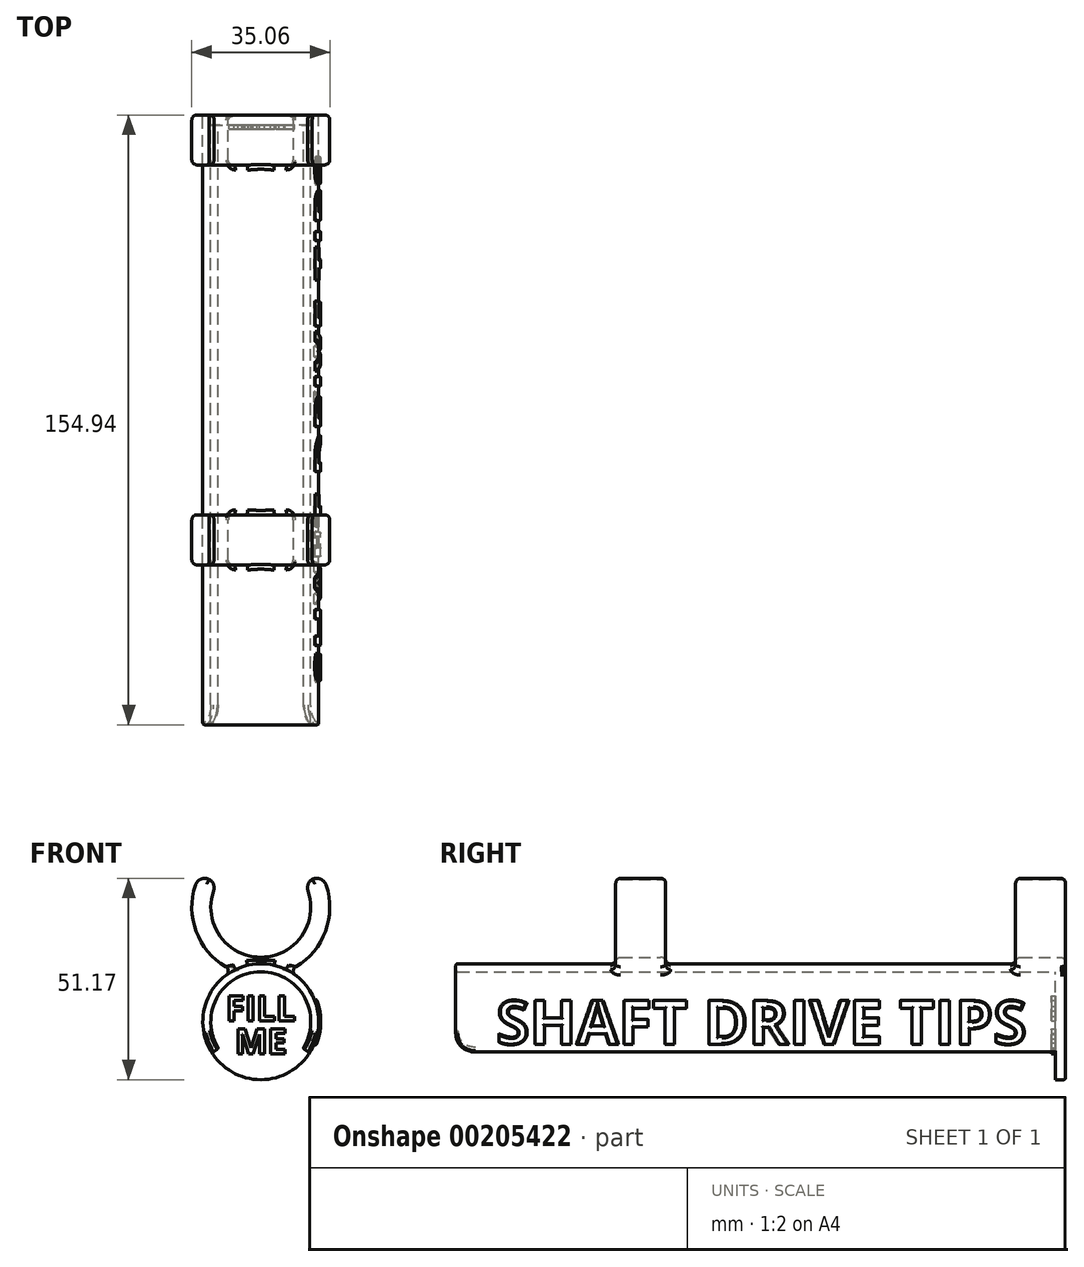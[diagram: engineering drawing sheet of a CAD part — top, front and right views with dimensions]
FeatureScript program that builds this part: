
annotation { "Feature Type Name" : "Feature", "Feature Type Description" : "" }
export const myFeature = defineFeature(function(context is Context, id is Id, definition is map)
    precondition{}
    {
        {
            var Q0;
            Q0=qCreatedBy(makeId("Front.planeOp"),FACE);
            var sketch = newSketch(context, id + "F0", { "sketchPlane" : qUnion([Q0])});
            skCircle(sketch, "E0", {"center": v(0, 0) * mm, "radius": 14.73 * mm});
            skSolve(sketch);
        }
        {
            var Q0;
            Q0 = qSketchRegion(id + "F0", true);
            extrude(context, id + "F1", {"entities" : qUnion([Q0]), "depth" : 2.54 * mm});
        }
        {
            var Q0;
            Q0=makeQuery(id+"F1.opExtrude","CAP_FACE",FACE,{"disambiguationData":[OSD([sQuery(id+"F0.wireOp",EDGE,"E0")])],"isStart":false});
            var sketch = newSketch(context, id + "F2", { "sketchPlane" : qUnion([Q0])});
            skArc(sketch, "E1", {"start": v(12.43, -7.91) * mm, "mid": v(0, 14.73) * mm, "end": v(-12.43, -7.91) * mm});
            skArc(sketch, "E2", {"start": v(10.71, -6.82) * mm, "mid": v(0, 12.7) * mm, "end": v(-10.71, -6.82) * mm});
            skLineSegment(sketch, "E3", {"start": v(-10.71, -6.82) * mm, "end": v(-12.43, -7.91) * mm});
            skLineSegment(sketch, "E4", {"start": v(12.43, -7.91) * mm, "end": v(10.71, -6.82) * mm});
            skSolve(sketch);
        }
        {
            var Q0;
            Q0 = qSketchRegion(id + "F2", true);
            extrude(context, id + "F3", {"entities" : qUnion([Q0]), "operationType" : NewBodyOperationType.ADD, "depth" : 152.4 * mm});
        }
        {
            var Q0;
            Q0=makeQuery(id+"F3.opExtrude","CAP_EDGE",EDGE,{"disambiguationData":[OSD([sQuery(id+"F2.wireOp",EDGE,"E3")])],"isStart":false});
            var Q1;
            Q1=makeQuery(id+"F3.opExtrude","CAP_EDGE",EDGE,{"disambiguationData":[OSD([sQuery(id+"F2.wireOp",EDGE,"E4")])],"isStart":false});
            fillet(context, id + "F4", {"entities" : qUnion([Q0, Q1]), "radius" : 5.08 * mm, "tangentPropagation" : true, "allowEdgeOverflow" : false});
        }
        {
            var Q0;
            Q0=qCreatedBy(makeId("Right.planeOp"),FACE);
            var sketch = newSketch(context, id + "F5", { "sketchPlane" : qUnion([Q0])});
            skText(sketch, "E5", { "text": "SHAFT DRIVE TIPS", "fontName": "OpenSans-Bold.ttf"});
            const initialGuessF5  = {"E5": [-0.14472, -0.00573, 1, 0, 0.01118]};
            skSetInitialGuess(sketch, initialGuessF5);
            skSolve(sketch);
        }
        {
            var Q0;
            Q0 = qSketchRegion(id + "F5", true);
            extrude(context, id + "F6", {"entities" : qUnion([Q0]), "operationType" : NewBodyOperationType.ADD, "depth" : 25.4 * mm});
        }
        {
            var Q0;
            Q0=makeQuery(id+"F1.opExtrude","CAP_FACE",FACE,{"disambiguationData":[OSD([sQuery(id+"F0.wireOp",EDGE,"E0")])],"isStart":false});
            var sketch = newSketch(context, id + "F7", { "sketchPlane" : qUnion([Q0])});
            skCircle(sketch, "E6", {"center": v(0, 0) * mm, "radius": 12.7 * mm});
            skSolve(sketch);
        }
        {
            var Q0;
            Q0 = qSketchRegion(id + "F7", true);
            extrude(context, id + "F8", {"entities" : qUnion([Q0]), "operationType" : NewBodyOperationType.REMOVE, "depth" : 177.8 * mm});
        }
        {
            var Q0;
            Q0=makeQuery(id+"F1.opExtrude","CAP_FACE",FACE,{"disambiguationData":[OSD([sQuery(id+"F0.wireOp",EDGE,"E0")])],"isStart":false});
            var sketch = newSketch(context, id + "F9", { "sketchPlane" : qUnion([Q0])});
            skCircle(sketch, "E7", {"center": v(0, 0) * mm, "radius": 15.24 * mm});
            skCircle(sketch, "E8", {"center": v(0, 0) * mm, "radius": 65.87 * mm});
            skSolve(sketch);
        }
        {
            var Q0;
            Q0 = qSketchRegion(id + "F9", true);
            extrude(context, id + "F10", {"entities" : qUnion([Q0]), "operationType" : NewBodyOperationType.REMOVE, "depth" : 152.4 * mm});
        }
        {
            var Q0;
            Q0=makeQuery(id+"F3.opExtrude","SWEPT_EDGE",EDGE,{"disambiguationData":[OSD([sQuery(id+"F2.wireOp",EDGE,"E2"),sQuery(id+"F2.wireOp",EDGE,"E3")])]});
            var Q1;
            Q1=makeQuery(id+"F4.opFillet","BLEND_EDGE",EDGE,{"blendedFrom":[makeQuery(id+"F3.opExtrude","CAP_EDGE",EDGE,{"disambiguationData":[OSD([sQuery(id+"F2.wireOp",EDGE,"E4")])],"isStart":false}),makeQuery(id+"F3.boolean.opBoolean","MERGE",FACE,{"derivedFrom":[makeQuery(id+"F1.opExtrude","SWEPT_FACE",FACE,{"disambiguationData":[OSD([sQuery(id+"F0.wireOp",EDGE,"E0")])]}),makeQuery(id+"F3.opExtrude","SWEPT_FACE",FACE,{"disambiguationData":[OSD([sQuery(id+"F2.wireOp",EDGE,"E1")])]})]})],"blendedInto":[makeQuery(id+"F3.boolean.opBoolean","MERGE",FACE,{"derivedFrom":[makeQuery(id+"F1.opExtrude","SWEPT_FACE",FACE,{"disambiguationData":[OSD([sQuery(id+"F0.wireOp",EDGE,"E0")])]}),makeQuery(id+"F3.opExtrude","SWEPT_FACE",FACE,{"disambiguationData":[OSD([sQuery(id+"F2.wireOp",EDGE,"E1")])]})]})]});
            var Q2;
            Q2=makeQuery(id+"F3.opExtrude","CAP_EDGE",EDGE,{"disambiguationData":[OSD([sQuery(id+"F2.wireOp",EDGE,"E2")])],"isStart":true});
            var Q3;
            Q3=makeQuery(id+"F1.opExtrude","CAP_EDGE",EDGE,{"disambiguationData":[OSD([sQuery(id+"F0.wireOp",EDGE,"E0")])],"isStart":true});
            fillet(context, id + "F11", {"entities" : qUnion([Q0, Q1, Q2, Q3]), "radius" : 0.5 * mm, "tangentPropagation" : true, "allowEdgeOverflow" : false});
        }
        {
            var Q0;
            Q0=qCreatedBy(makeId("Front.planeOp"),FACE);
            cPlane(context, id + "F12", {"entities" : qUnion([Q0]), "cplaneType" : CPlaneType.OFFSET, "offset" : 101.6 * mm, "width" : 152.4 * mm, "height" : 152.4 * mm});
        }
        {
            var Q0;
            Q0=qCreatedBy(makeId("Front.planeOp"),FACE);
            var sketch = newSketch(context, id + "F13", { "sketchPlane" : qUnion([Q0])});
            skArc(sketch, "E9", {"start": v(-11.15, 35.14) * mm, "mid": v(0, 16.37) * mm, "end": v(11.15, 35.14) * mm});
            skArc(sketch, "E10", {"start": v(5.72, 12.5) * mm, "mid": v(16.34, 22.73) * mm, "end": v(15.4, 37.45) * mm});
            skArc(sketch, "E11", {"start": v(5.72, 12.5) * mm, "mid": v(0, 13.74) * mm, "end": v(-5.72, 12.5) * mm});
            skLineSegment(sketch, "E12", {"start": v(-11.15, 35.14) * mm, "end": v(-15.4, 37.45) * mm});
            skLineSegment(sketch, "E13", {"start": v(15.4, 37.45) * mm, "end": v(11.15, 35.14) * mm});
            skArc(sketch, "E14.trimOffspring", {"start": v(-15.4, 37.45) * mm, "mid": v(-16.34, 22.73) * mm, "end": v(-5.72, 12.5) * mm});
            skSolve(sketch);
        }
        {
            var Q0;
            Q0 = qSketchRegion(id + "F13", true);
            extrude(context, id + "F14", {"entities" : qUnion([Q0]), "operationType" : NewBodyOperationType.ADD, "depth" : 114.3 * mm});
        }
        {
            var Q0;
            Q0=qCreatedBy(id+"F12.planeOp",FACE);
            var sketch = newSketch(context, id + "F15", { "sketchPlane" : qUnion([Q0])});
            skArc(sketch, "E15", {"start": v(8.99, 11.67) * mm, "mid": v(0, 14.73) * mm, "end": v(-8.99, 11.67) * mm});
            skLineSegment(sketch, "E16.bottom", {"start": v(-19.66, 38.88) * mm, "end": v(20.71, 38.88) * mm});
            skLineSegment(sketch, "E16.top", {"start": v(-19.66, 11.67) * mm, "end": v(-8.99, 11.67) * mm});
            skLineSegment(sketch, "E16.left", {"start": v(-19.66, 38.88) * mm, "end": v(-19.66, 11.67) * mm});
            skLineSegment(sketch, "E16.right", {"start": v(20.71, 38.88) * mm, "end": v(20.71, 11.67) * mm});
            skLineSegment(sketch, "E17.trimOffspring", {"start": v(8.99, 11.67) * mm, "end": v(20.71, 11.67) * mm});
            skSolve(sketch);
        }
        {
            var Q0;
            Q0 = qSketchRegion(id + "F15", true);
            extrude(context, id + "F16", {"entities" : qUnion([Q0]), "operationType" : NewBodyOperationType.REMOVE, "oppositeDirection" : true, "depth" : 88.9 * mm});
        }
        {
            var Q0;
            {var subQ0=sQuery(id+"F13.wireOp",EDGE,"E9");var subQ1=sQuery(id+"F13.wireOp",EDGE,"E12");Q0=makeQuery(id+"F16.boolean.opBoolean","SPLIT",EDGE,{"disambiguationData":[TD([makeQuery(id+"F14.opExtrude","CAP_FACE",FACE,{"disambiguationData":[OSD([subQ0,sQuery(id+"F13.wireOp",EDGE,"E10"),sQuery(id+"F13.wireOp",EDGE,"E11"),subQ1,sQuery(id+"F13.wireOp",EDGE,"E13"),sQuery(id+"F13.wireOp",EDGE,"E14.trimOffspring")])],"isStart":false})])],"derivedFrom":makeQuery(id+"F14.opExtrude","SWEPT_EDGE",EDGE,{"disambiguationData":[OSD([subQ0,subQ1])]})});}
            var Q1;
            {var subQ0=sQuery(id+"F13.wireOp",EDGE,"E14.trimOffspring");var subQ1=sQuery(id+"F13.wireOp",EDGE,"E12");Q1=makeQuery(id+"F16.boolean.opBoolean","SPLIT",EDGE,{"disambiguationData":[TD([makeQuery(id+"F14.opExtrude","CAP_FACE",FACE,{"disambiguationData":[OSD([sQuery(id+"F13.wireOp",EDGE,"E9"),sQuery(id+"F13.wireOp",EDGE,"E10"),sQuery(id+"F13.wireOp",EDGE,"E11"),subQ1,sQuery(id+"F13.wireOp",EDGE,"E13"),subQ0])],"isStart":false})])],"derivedFrom":makeQuery(id+"F14.opExtrude","SWEPT_EDGE",EDGE,{"disambiguationData":[OSD([subQ1,subQ0])]})});}
            var Q2;
            {var subQ0=sQuery(id+"F13.wireOp",EDGE,"E13");var subQ1=sQuery(id+"F13.wireOp",EDGE,"E10");Q2=makeQuery(id+"F16.boolean.opBoolean","SPLIT",EDGE,{"disambiguationData":[TD([makeQuery(id+"F14.opExtrude","CAP_FACE",FACE,{"disambiguationData":[OSD([sQuery(id+"F13.wireOp",EDGE,"E9"),subQ1,sQuery(id+"F13.wireOp",EDGE,"E11"),sQuery(id+"F13.wireOp",EDGE,"E12"),subQ0,sQuery(id+"F13.wireOp",EDGE,"E14.trimOffspring")])],"isStart":false})])],"derivedFrom":makeQuery(id+"F14.opExtrude","SWEPT_EDGE",EDGE,{"disambiguationData":[OSD([subQ1,subQ0])]})});}
            var Q3;
            {var subQ0=sQuery(id+"F13.wireOp",EDGE,"E9");var subQ1=sQuery(id+"F13.wireOp",EDGE,"E13");Q3=makeQuery(id+"F16.boolean.opBoolean","SPLIT",EDGE,{"disambiguationData":[TD([makeQuery(id+"F14.opExtrude","CAP_FACE",FACE,{"disambiguationData":[OSD([subQ0,sQuery(id+"F13.wireOp",EDGE,"E10"),sQuery(id+"F13.wireOp",EDGE,"E11"),sQuery(id+"F13.wireOp",EDGE,"E12"),subQ1,sQuery(id+"F13.wireOp",EDGE,"E14.trimOffspring")])],"isStart":false})])],"derivedFrom":makeQuery(id+"F14.opExtrude","SWEPT_EDGE",EDGE,{"disambiguationData":[OSD([subQ0,subQ1])]})});}
            var Q4;
            {var subQ0=sQuery(id+"F13.wireOp",EDGE,"E13");var subQ1=sQuery(id+"F13.wireOp",EDGE,"E9");Q4=makeQuery(id+"F16.boolean.opBoolean","SPLIT",EDGE,{"disambiguationData":[TD([makeQuery(id+"F1.opExtrude","CAP_FACE",FACE,{"disambiguationData":[OSD([sQuery(id+"F0.wireOp",EDGE,"E0")])],"isStart":true})])],"derivedFrom":makeQuery(id+"F14.opExtrude","SWEPT_EDGE",EDGE,{"disambiguationData":[OSD([subQ1,subQ0])]})});}
            var Q5;
            {var subQ0=sQuery(id+"F13.wireOp",EDGE,"E10");var subQ1=sQuery(id+"F13.wireOp",EDGE,"E13");Q5=makeQuery(id+"F16.boolean.opBoolean","SPLIT",EDGE,{"disambiguationData":[TD([makeQuery(id+"F1.opExtrude","CAP_FACE",FACE,{"disambiguationData":[OSD([sQuery(id+"F0.wireOp",EDGE,"E0")])],"isStart":true})])],"derivedFrom":makeQuery(id+"F14.opExtrude","SWEPT_EDGE",EDGE,{"disambiguationData":[OSD([subQ0,subQ1])]})});}
            var Q6;
            {var subQ0=sQuery(id+"F13.wireOp",EDGE,"E14.trimOffspring");var subQ1=sQuery(id+"F13.wireOp",EDGE,"E12");Q6=makeQuery(id+"F16.boolean.opBoolean","SPLIT",EDGE,{"disambiguationData":[TD([makeQuery(id+"F1.opExtrude","CAP_FACE",FACE,{"disambiguationData":[OSD([sQuery(id+"F0.wireOp",EDGE,"E0")])],"isStart":true})])],"derivedFrom":makeQuery(id+"F14.opExtrude","SWEPT_EDGE",EDGE,{"disambiguationData":[OSD([subQ1,subQ0])]})});}
            var Q7;
            {var subQ0=sQuery(id+"F13.wireOp",EDGE,"E12");var subQ1=sQuery(id+"F13.wireOp",EDGE,"E9");Q7=makeQuery(id+"F16.boolean.opBoolean","SPLIT",EDGE,{"disambiguationData":[TD([makeQuery(id+"F1.opExtrude","CAP_FACE",FACE,{"disambiguationData":[OSD([sQuery(id+"F0.wireOp",EDGE,"E0")])],"isStart":true})])],"derivedFrom":makeQuery(id+"F14.opExtrude","SWEPT_EDGE",EDGE,{"disambiguationData":[OSD([subQ1,subQ0])]})});}
            fillet(context, id + "F17", {"entities" : qUnion([Q0, Q1, Q2, Q3, Q4, Q5, Q6, Q7]), "radius" : 2.54 * mm, "tangentPropagation" : true, "allowEdgeOverflow" : false});
        }
        {
            var Q0;
            Q0=makeQuery(id+"F16.boolean.opBoolean","INTERSECT",EDGE,{"derivedFrom":[makeQuery(id+"F14.opExtrude","SWEPT_FACE",FACE,{"disambiguationData":[OSD([sQuery(id+"F13.wireOp",EDGE,"E9")])]}),makeQuery(id+"F16.opExtrude","CAP_FACE",FACE,{"disambiguationData":[OSD([sQuery(id+"F15.wireOp",EDGE,"E15"),sQuery(id+"F15.wireOp",EDGE,"E16.bottom"),sQuery(id+"F15.wireOp",EDGE,"E16.top"),sQuery(id+"F15.wireOp",EDGE,"E16.left"),sQuery(id+"F15.wireOp",EDGE,"E16.right"),sQuery(id+"F15.wireOp",EDGE,"E17.trimOffspring")])],"isStart":false})]});
            var Q1;
            {var subQ0=makeQuery(id+"F16.opExtrude","CAP_FACE",FACE,{"disambiguationData":[OSD([sQuery(id+"F15.wireOp",EDGE,"E15"),sQuery(id+"F15.wireOp",EDGE,"E16.bottom"),sQuery(id+"F15.wireOp",EDGE,"E16.top"),sQuery(id+"F15.wireOp",EDGE,"E16.left"),sQuery(id+"F15.wireOp",EDGE,"E16.right"),sQuery(id+"F15.wireOp",EDGE,"E17.trimOffspring")])],"isStart":false});var subQ1=sQuery(id+"F13.wireOp",EDGE,"E13");var subQ2=sQuery(id+"F13.wireOp",EDGE,"E9");Q1=makeQuery(id+"F17.opFillet","BLEND_EDGE",EDGE,{"blendedFrom":[makeQuery(id+"F16.boolean.opBoolean","SPLIT",EDGE,{"disambiguationData":[TD([makeQuery(id+"F1.opExtrude","CAP_FACE",FACE,{"disambiguationData":[OSD([sQuery(id+"F0.wireOp",EDGE,"E0")])],"isStart":true})])],"derivedFrom":makeQuery(id+"F14.opExtrude","SWEPT_EDGE",EDGE,{"disambiguationData":[OSD([subQ2,subQ1])]})}),makeQuery(id+"F16.boolean.opBoolean","COPY",FACE,{"derivedFrom":subQ0})],"blendedInto":[makeQuery(id+"F16.boolean.opBoolean","COPY",FACE,{"derivedFrom":subQ0})]});}
            var Q2;
            Q2=makeQuery(id+"F16.boolean.opBoolean","INTERSECT",EDGE,{"derivedFrom":[makeQuery(id+"F14.opExtrude","SWEPT_FACE",FACE,{"disambiguationData":[OSD([sQuery(id+"F13.wireOp",EDGE,"E10")])]}),makeQuery(id+"F16.opExtrude","CAP_FACE",FACE,{"disambiguationData":[OSD([sQuery(id+"F15.wireOp",EDGE,"E15"),sQuery(id+"F15.wireOp",EDGE,"E16.bottom"),sQuery(id+"F15.wireOp",EDGE,"E16.top"),sQuery(id+"F15.wireOp",EDGE,"E16.left"),sQuery(id+"F15.wireOp",EDGE,"E16.right"),sQuery(id+"F15.wireOp",EDGE,"E17.trimOffspring")])],"isStart":false})]});
            var Q3;
            {var subQ0=makeQuery(id+"F16.opExtrude","CAP_FACE",FACE,{"disambiguationData":[OSD([sQuery(id+"F15.wireOp",EDGE,"E15"),sQuery(id+"F15.wireOp",EDGE,"E16.bottom"),sQuery(id+"F15.wireOp",EDGE,"E16.top"),sQuery(id+"F15.wireOp",EDGE,"E16.left"),sQuery(id+"F15.wireOp",EDGE,"E16.right"),sQuery(id+"F15.wireOp",EDGE,"E17.trimOffspring")])],"isStart":false});var subQ1=sQuery(id+"F13.wireOp",EDGE,"E10");var subQ2=sQuery(id+"F13.wireOp",EDGE,"E13");Q3=makeQuery(id+"F17.opFillet","BLEND_EDGE",EDGE,{"blendedFrom":[makeQuery(id+"F16.boolean.opBoolean","SPLIT",EDGE,{"disambiguationData":[TD([makeQuery(id+"F1.opExtrude","CAP_FACE",FACE,{"disambiguationData":[OSD([sQuery(id+"F0.wireOp",EDGE,"E0")])],"isStart":true})])],"derivedFrom":makeQuery(id+"F14.opExtrude","SWEPT_EDGE",EDGE,{"disambiguationData":[OSD([subQ1,subQ2])]})}),makeQuery(id+"F16.boolean.opBoolean","COPY",FACE,{"derivedFrom":subQ0})],"blendedInto":[makeQuery(id+"F16.boolean.opBoolean","COPY",FACE,{"derivedFrom":subQ0})]});}
            var Q4;
            {var subQ0=makeQuery(id+"F16.opExtrude","CAP_FACE",FACE,{"disambiguationData":[OSD([sQuery(id+"F15.wireOp",EDGE,"E15"),sQuery(id+"F15.wireOp",EDGE,"E16.bottom"),sQuery(id+"F15.wireOp",EDGE,"E16.top"),sQuery(id+"F15.wireOp",EDGE,"E16.left"),sQuery(id+"F15.wireOp",EDGE,"E16.right"),sQuery(id+"F15.wireOp",EDGE,"E17.trimOffspring")])],"isStart":false});var subQ1=sQuery(id+"F13.wireOp",EDGE,"E12");var subQ2=sQuery(id+"F13.wireOp",EDGE,"E9");Q4=makeQuery(id+"F17.opFillet","BLEND_EDGE",EDGE,{"blendedFrom":[makeQuery(id+"F16.boolean.opBoolean","SPLIT",EDGE,{"disambiguationData":[TD([makeQuery(id+"F1.opExtrude","CAP_FACE",FACE,{"disambiguationData":[OSD([sQuery(id+"F0.wireOp",EDGE,"E0")])],"isStart":true})])],"derivedFrom":makeQuery(id+"F14.opExtrude","SWEPT_EDGE",EDGE,{"disambiguationData":[OSD([subQ2,subQ1])]})}),makeQuery(id+"F16.boolean.opBoolean","COPY",FACE,{"derivedFrom":subQ0})],"blendedInto":[makeQuery(id+"F16.boolean.opBoolean","COPY",FACE,{"derivedFrom":subQ0})]});}
            var Q5;
            Q5=makeQuery(id+"F16.boolean.opBoolean","INTERSECT",EDGE,{"derivedFrom":[makeQuery(id+"F14.opExtrude","SWEPT_FACE",FACE,{"disambiguationData":[OSD([sQuery(id+"F13.wireOp",EDGE,"E14.trimOffspring")])]}),makeQuery(id+"F16.opExtrude","CAP_FACE",FACE,{"disambiguationData":[OSD([sQuery(id+"F15.wireOp",EDGE,"E15"),sQuery(id+"F15.wireOp",EDGE,"E16.bottom"),sQuery(id+"F15.wireOp",EDGE,"E16.top"),sQuery(id+"F15.wireOp",EDGE,"E16.left"),sQuery(id+"F15.wireOp",EDGE,"E16.right"),sQuery(id+"F15.wireOp",EDGE,"E17.trimOffspring")])],"isStart":false})]});
            var Q6;
            Q6=makeQuery(id+"F14.opExtrude","CAP_EDGE",EDGE,{"disambiguationData":[OSD([sQuery(id+"F13.wireOp",EDGE,"E10")])],"isStart":true});
            var Q7;
            {var subQ0=sQuery(id+"F13.wireOp",EDGE,"E13");var subQ1=sQuery(id+"F13.wireOp",EDGE,"E10");var subQ2=makeQuery(id+"F14.opExtrude","CAP_FACE",FACE,{"disambiguationData":[OSD([sQuery(id+"F13.wireOp",EDGE,"E9"),subQ1,sQuery(id+"F13.wireOp",EDGE,"E11"),sQuery(id+"F13.wireOp",EDGE,"E12"),subQ0,sQuery(id+"F13.wireOp",EDGE,"E14.trimOffspring")])],"isStart":true});var subQ3=makeQuery(id+"F1.opExtrude","CAP_FACE",FACE,{"disambiguationData":[OSD([sQuery(id+"F0.wireOp",EDGE,"E0")])],"isStart":true});Q7=makeQuery(id+"F17.opFillet","BLEND_EDGE",EDGE,{"blendedFrom":[makeQuery(id+"F16.boolean.opBoolean","SPLIT",EDGE,{"disambiguationData":[TD([subQ3])],"derivedFrom":makeQuery(id+"F14.opExtrude","SWEPT_EDGE",EDGE,{"disambiguationData":[OSD([subQ1,subQ0])]})}),makeQuery(id+"F14.boolean.opBoolean","MERGE",FACE,{"derivedFrom":[subQ3,subQ2]})],"blendedInto":[makeQuery(id+"F14.boolean.opBoolean","MERGE",FACE,{"derivedFrom":[subQ3,subQ2]})]});}
            var Q8;
            {var subQ0=sQuery(id+"F13.wireOp",EDGE,"E13");var subQ1=sQuery(id+"F13.wireOp",EDGE,"E9");var subQ2=makeQuery(id+"F14.opExtrude","CAP_FACE",FACE,{"disambiguationData":[OSD([subQ1,sQuery(id+"F13.wireOp",EDGE,"E10"),sQuery(id+"F13.wireOp",EDGE,"E11"),sQuery(id+"F13.wireOp",EDGE,"E12"),subQ0,sQuery(id+"F13.wireOp",EDGE,"E14.trimOffspring")])],"isStart":true});var subQ3=makeQuery(id+"F1.opExtrude","CAP_FACE",FACE,{"disambiguationData":[OSD([sQuery(id+"F0.wireOp",EDGE,"E0")])],"isStart":true});Q8=makeQuery(id+"F17.opFillet","BLEND_EDGE",EDGE,{"blendedFrom":[makeQuery(id+"F16.boolean.opBoolean","SPLIT",EDGE,{"disambiguationData":[TD([subQ3])],"derivedFrom":makeQuery(id+"F14.opExtrude","SWEPT_EDGE",EDGE,{"disambiguationData":[OSD([subQ1,subQ0])]})}),makeQuery(id+"F14.boolean.opBoolean","MERGE",FACE,{"derivedFrom":[subQ3,subQ2]})],"blendedInto":[makeQuery(id+"F14.boolean.opBoolean","MERGE",FACE,{"derivedFrom":[subQ3,subQ2]})]});}
            var Q9;
            Q9=makeQuery(id+"F14.opExtrude","CAP_EDGE",EDGE,{"disambiguationData":[OSD([sQuery(id+"F13.wireOp",EDGE,"E9")])],"isStart":true});
            var Q10;
            {var subQ0=sQuery(id+"F13.wireOp",EDGE,"E12");var subQ1=sQuery(id+"F13.wireOp",EDGE,"E9");var subQ2=makeQuery(id+"F14.opExtrude","CAP_FACE",FACE,{"disambiguationData":[OSD([subQ1,sQuery(id+"F13.wireOp",EDGE,"E10"),sQuery(id+"F13.wireOp",EDGE,"E11"),subQ0,sQuery(id+"F13.wireOp",EDGE,"E13"),sQuery(id+"F13.wireOp",EDGE,"E14.trimOffspring")])],"isStart":true});var subQ3=makeQuery(id+"F1.opExtrude","CAP_FACE",FACE,{"disambiguationData":[OSD([sQuery(id+"F0.wireOp",EDGE,"E0")])],"isStart":true});Q10=makeQuery(id+"F17.opFillet","BLEND_EDGE",EDGE,{"blendedFrom":[makeQuery(id+"F16.boolean.opBoolean","SPLIT",EDGE,{"disambiguationData":[TD([subQ3])],"derivedFrom":makeQuery(id+"F14.opExtrude","SWEPT_EDGE",EDGE,{"disambiguationData":[OSD([subQ1,subQ0])]})}),makeQuery(id+"F14.boolean.opBoolean","MERGE",FACE,{"derivedFrom":[subQ3,subQ2]})],"blendedInto":[makeQuery(id+"F14.boolean.opBoolean","MERGE",FACE,{"derivedFrom":[subQ3,subQ2]})]});}
            var Q11;
            Q11=makeQuery(id+"F14.opExtrude","CAP_EDGE",EDGE,{"disambiguationData":[OSD([sQuery(id+"F13.wireOp",EDGE,"E14.trimOffspring")])],"isStart":true});
            var Q12;
            Q12=makeQuery(id+"F16.boolean.opBoolean","INTERSECT",EDGE,{"derivedFrom":[makeQuery(id+"F14.opExtrude","SWEPT_FACE",FACE,{"disambiguationData":[OSD([sQuery(id+"F13.wireOp",EDGE,"E10")])]}),makeQuery(id+"F16.opExtrude","CAP_FACE",FACE,{"disambiguationData":[OSD([sQuery(id+"F15.wireOp",EDGE,"E15"),sQuery(id+"F15.wireOp",EDGE,"E16.bottom"),sQuery(id+"F15.wireOp",EDGE,"E16.top"),sQuery(id+"F15.wireOp",EDGE,"E16.left"),sQuery(id+"F15.wireOp",EDGE,"E16.right"),sQuery(id+"F15.wireOp",EDGE,"E17.trimOffspring")])],"isStart":true})]});
            var Q13;
            {var subQ0=makeQuery(id+"F16.opExtrude","CAP_FACE",FACE,{"disambiguationData":[OSD([sQuery(id+"F15.wireOp",EDGE,"E15"),sQuery(id+"F15.wireOp",EDGE,"E16.bottom"),sQuery(id+"F15.wireOp",EDGE,"E16.top"),sQuery(id+"F15.wireOp",EDGE,"E16.left"),sQuery(id+"F15.wireOp",EDGE,"E16.right"),sQuery(id+"F15.wireOp",EDGE,"E17.trimOffspring")])],"isStart":true});var subQ1=sQuery(id+"F13.wireOp",EDGE,"E13");var subQ2=sQuery(id+"F13.wireOp",EDGE,"E10");Q13=makeQuery(id+"F17.opFillet","BLEND_EDGE",EDGE,{"blendedFrom":[makeQuery(id+"F16.boolean.opBoolean","SPLIT",EDGE,{"disambiguationData":[TD([makeQuery(id+"F14.opExtrude","CAP_FACE",FACE,{"disambiguationData":[OSD([sQuery(id+"F13.wireOp",EDGE,"E9"),subQ2,sQuery(id+"F13.wireOp",EDGE,"E11"),sQuery(id+"F13.wireOp",EDGE,"E12"),subQ1,sQuery(id+"F13.wireOp",EDGE,"E14.trimOffspring")])],"isStart":false})])],"derivedFrom":makeQuery(id+"F14.opExtrude","SWEPT_EDGE",EDGE,{"disambiguationData":[OSD([subQ2,subQ1])]})}),makeQuery(id+"F16.boolean.opBoolean","COPY",FACE,{"derivedFrom":subQ0})],"blendedInto":[makeQuery(id+"F16.boolean.opBoolean","COPY",FACE,{"derivedFrom":subQ0})]});}
            var Q14;
            {var subQ0=makeQuery(id+"F16.opExtrude","CAP_FACE",FACE,{"disambiguationData":[OSD([sQuery(id+"F15.wireOp",EDGE,"E15"),sQuery(id+"F15.wireOp",EDGE,"E16.bottom"),sQuery(id+"F15.wireOp",EDGE,"E16.top"),sQuery(id+"F15.wireOp",EDGE,"E16.left"),sQuery(id+"F15.wireOp",EDGE,"E16.right"),sQuery(id+"F15.wireOp",EDGE,"E17.trimOffspring")])],"isStart":true});var subQ1=sQuery(id+"F13.wireOp",EDGE,"E9");var subQ2=sQuery(id+"F13.wireOp",EDGE,"E13");Q14=makeQuery(id+"F17.opFillet","BLEND_EDGE",EDGE,{"blendedFrom":[makeQuery(id+"F16.boolean.opBoolean","SPLIT",EDGE,{"disambiguationData":[TD([makeQuery(id+"F14.opExtrude","CAP_FACE",FACE,{"disambiguationData":[OSD([subQ1,sQuery(id+"F13.wireOp",EDGE,"E10"),sQuery(id+"F13.wireOp",EDGE,"E11"),sQuery(id+"F13.wireOp",EDGE,"E12"),subQ2,sQuery(id+"F13.wireOp",EDGE,"E14.trimOffspring")])],"isStart":false})])],"derivedFrom":makeQuery(id+"F14.opExtrude","SWEPT_EDGE",EDGE,{"disambiguationData":[OSD([subQ1,subQ2])]})}),makeQuery(id+"F16.boolean.opBoolean","COPY",FACE,{"derivedFrom":subQ0})],"blendedInto":[makeQuery(id+"F16.boolean.opBoolean","COPY",FACE,{"derivedFrom":subQ0})]});}
            var Q15;
            Q15=makeQuery(id+"F16.boolean.opBoolean","INTERSECT",EDGE,{"derivedFrom":[makeQuery(id+"F14.opExtrude","SWEPT_FACE",FACE,{"disambiguationData":[OSD([sQuery(id+"F13.wireOp",EDGE,"E9")])]}),makeQuery(id+"F16.opExtrude","CAP_FACE",FACE,{"disambiguationData":[OSD([sQuery(id+"F15.wireOp",EDGE,"E15"),sQuery(id+"F15.wireOp",EDGE,"E16.bottom"),sQuery(id+"F15.wireOp",EDGE,"E16.top"),sQuery(id+"F15.wireOp",EDGE,"E16.left"),sQuery(id+"F15.wireOp",EDGE,"E16.right"),sQuery(id+"F15.wireOp",EDGE,"E17.trimOffspring")])],"isStart":true})]});
            var Q16;
            {var subQ0=makeQuery(id+"F16.opExtrude","CAP_FACE",FACE,{"disambiguationData":[OSD([sQuery(id+"F15.wireOp",EDGE,"E15"),sQuery(id+"F15.wireOp",EDGE,"E16.bottom"),sQuery(id+"F15.wireOp",EDGE,"E16.top"),sQuery(id+"F15.wireOp",EDGE,"E16.left"),sQuery(id+"F15.wireOp",EDGE,"E16.right"),sQuery(id+"F15.wireOp",EDGE,"E17.trimOffspring")])],"isStart":true});var subQ1=sQuery(id+"F13.wireOp",EDGE,"E9");var subQ2=sQuery(id+"F13.wireOp",EDGE,"E12");Q16=makeQuery(id+"F17.opFillet","BLEND_EDGE",EDGE,{"blendedFrom":[makeQuery(id+"F16.boolean.opBoolean","SPLIT",EDGE,{"disambiguationData":[TD([makeQuery(id+"F14.opExtrude","CAP_FACE",FACE,{"disambiguationData":[OSD([subQ1,sQuery(id+"F13.wireOp",EDGE,"E10"),sQuery(id+"F13.wireOp",EDGE,"E11"),subQ2,sQuery(id+"F13.wireOp",EDGE,"E13"),sQuery(id+"F13.wireOp",EDGE,"E14.trimOffspring")])],"isStart":false})])],"derivedFrom":makeQuery(id+"F14.opExtrude","SWEPT_EDGE",EDGE,{"disambiguationData":[OSD([subQ1,subQ2])]})}),makeQuery(id+"F16.boolean.opBoolean","COPY",FACE,{"derivedFrom":subQ0})],"blendedInto":[makeQuery(id+"F16.boolean.opBoolean","COPY",FACE,{"derivedFrom":subQ0})]});}
            var Q17;
            Q17=makeQuery(id+"F16.boolean.opBoolean","INTERSECT",EDGE,{"derivedFrom":[makeQuery(id+"F14.opExtrude","SWEPT_FACE",FACE,{"disambiguationData":[OSD([sQuery(id+"F13.wireOp",EDGE,"E14.trimOffspring")])]}),makeQuery(id+"F16.opExtrude","CAP_FACE",FACE,{"disambiguationData":[OSD([sQuery(id+"F15.wireOp",EDGE,"E15"),sQuery(id+"F15.wireOp",EDGE,"E16.bottom"),sQuery(id+"F15.wireOp",EDGE,"E16.top"),sQuery(id+"F15.wireOp",EDGE,"E16.left"),sQuery(id+"F15.wireOp",EDGE,"E16.right"),sQuery(id+"F15.wireOp",EDGE,"E17.trimOffspring")])],"isStart":true})]});
            var Q18;
            Q18=makeQuery(id+"F14.opExtrude","CAP_EDGE",EDGE,{"disambiguationData":[OSD([sQuery(id+"F13.wireOp",EDGE,"E14.trimOffspring")])],"isStart":false});
            var Q19;
            {var subQ0=sQuery(id+"F13.wireOp",EDGE,"E14.trimOffspring");var subQ1=sQuery(id+"F13.wireOp",EDGE,"E12");var subQ2=makeQuery(id+"F14.opExtrude","CAP_FACE",FACE,{"disambiguationData":[OSD([sQuery(id+"F13.wireOp",EDGE,"E9"),sQuery(id+"F13.wireOp",EDGE,"E10"),sQuery(id+"F13.wireOp",EDGE,"E11"),subQ1,sQuery(id+"F13.wireOp",EDGE,"E13"),subQ0])],"isStart":false});Q19=makeQuery(id+"F17.opFillet","BLEND_EDGE",EDGE,{"blendedFrom":[makeQuery(id+"F16.boolean.opBoolean","SPLIT",EDGE,{"disambiguationData":[TD([subQ2])],"derivedFrom":makeQuery(id+"F14.opExtrude","SWEPT_EDGE",EDGE,{"disambiguationData":[OSD([subQ1,subQ0])]})}),subQ2],"blendedInto":[subQ2]});}
            var Q20;
            Q20=makeQuery(id+"F14.opExtrude","CAP_EDGE",EDGE,{"disambiguationData":[OSD([sQuery(id+"F13.wireOp",EDGE,"E9")])],"isStart":false});
            var Q21;
            {var subQ0=sQuery(id+"F13.wireOp",EDGE,"E12");var subQ1=sQuery(id+"F13.wireOp",EDGE,"E9");var subQ2=makeQuery(id+"F14.opExtrude","CAP_FACE",FACE,{"disambiguationData":[OSD([subQ1,sQuery(id+"F13.wireOp",EDGE,"E10"),sQuery(id+"F13.wireOp",EDGE,"E11"),subQ0,sQuery(id+"F13.wireOp",EDGE,"E13"),sQuery(id+"F13.wireOp",EDGE,"E14.trimOffspring")])],"isStart":false});Q21=makeQuery(id+"F17.opFillet","BLEND_EDGE",EDGE,{"blendedFrom":[makeQuery(id+"F16.boolean.opBoolean","SPLIT",EDGE,{"disambiguationData":[TD([subQ2])],"derivedFrom":makeQuery(id+"F14.opExtrude","SWEPT_EDGE",EDGE,{"disambiguationData":[OSD([subQ1,subQ0])]})}),subQ2],"blendedInto":[subQ2]});}
            var Q22;
            {var subQ0=sQuery(id+"F13.wireOp",EDGE,"E13");var subQ1=sQuery(id+"F13.wireOp",EDGE,"E9");var subQ2=makeQuery(id+"F14.opExtrude","CAP_FACE",FACE,{"disambiguationData":[OSD([subQ1,sQuery(id+"F13.wireOp",EDGE,"E10"),sQuery(id+"F13.wireOp",EDGE,"E11"),sQuery(id+"F13.wireOp",EDGE,"E12"),subQ0,sQuery(id+"F13.wireOp",EDGE,"E14.trimOffspring")])],"isStart":false});Q22=makeQuery(id+"F17.opFillet","BLEND_EDGE",EDGE,{"blendedFrom":[makeQuery(id+"F16.boolean.opBoolean","SPLIT",EDGE,{"disambiguationData":[TD([subQ2])],"derivedFrom":makeQuery(id+"F14.opExtrude","SWEPT_EDGE",EDGE,{"disambiguationData":[OSD([subQ1,subQ0])]})}),subQ2],"blendedInto":[subQ2]});}
            var Q23;
            Q23=makeQuery(id+"F14.opExtrude","CAP_EDGE",EDGE,{"disambiguationData":[OSD([sQuery(id+"F13.wireOp",EDGE,"E10")])],"isStart":false});
            fillet(context, id + "F18", {"entities" : qUnion([Q0, Q1, Q2, Q3, Q4, Q5, Q6, Q7, Q8, Q9, Q10, Q11, Q12, Q13, Q14, Q15, Q16, Q17, Q18, Q19, Q20, Q21, Q22, Q23]), "radius" : 1.27 * mm, "tangentPropagation" : true, "allowEdgeOverflow" : false});
        }
        {
            var Q0;
            {var subQ2=sQuery(id+"F2.wireOp",EDGE,"E1");var subQ3=sQuery(id+"F0.wireOp",EDGE,"E0");Q0=makeQuery(id+"F14.boolean.opBoolean","INTERSECT",EDGE,{"derivedFrom":[makeQuery(id+"F6.boolean.opBoolean","SPLIT",FACE,{"disambiguationData":[TD([makeQuery(id+"F1.opExtrude","CAP_FACE",FACE,{"disambiguationData":[OSD([subQ3])],"isStart":true})])],"derivedFrom":makeQuery(id+"F3.boolean.opBoolean","MERGE",FACE,{"derivedFrom":[makeQuery(id+"F1.opExtrude","SWEPT_FACE",FACE,{"disambiguationData":[OSD([subQ3])]}),makeQuery(id+"F3.opExtrude","SWEPT_FACE",FACE,{"disambiguationData":[OSD([subQ2])]})]})}),makeQuery(id+"F14.opExtrude","CAP_FACE",FACE,{"disambiguationData":[OSD([sQuery(id+"F13.wireOp",EDGE,"E9"),sQuery(id+"F13.wireOp",EDGE,"E10"),sQuery(id+"F13.wireOp",EDGE,"E11"),sQuery(id+"F13.wireOp",EDGE,"E12"),sQuery(id+"F13.wireOp",EDGE,"E13"),sQuery(id+"F13.wireOp",EDGE,"E14.trimOffspring")])],"isStart":false})]});}
            var Q1;
            Q1=makeQuery(id+"F16.boolean.opBoolean","COPY",EDGE,{"derivedFrom":makeQuery(id+"F16.opExtrude","CAP_EDGE",EDGE,{"disambiguationData":[OSD([sQuery(id+"F15.wireOp",EDGE,"E15")])],"isStart":false})});
            fillet(context, id + "F19", {"entities" : qUnion([Q0, Q1]), "radius" : 1.27 * mm, "tangentPropagation" : true, "allowEdgeOverflow" : false});
        }
        {
            var Q0;
            Q0=makeQuery(id+"F10.boolean.opBoolean","COPY",FACE,{"disambiguationData":[TD([makeQuery(id+"F6.opExtrude","SWEPT_FACE",FACE,{"disambiguationData":[OSD([sQuery(id+"F5.wireOp",EDGE,"E5.sketch_text.stroke-0")])]})])],"derivedFrom":makeQuery(id+"F10.opExtrude","SWEPT_FACE",FACE,{"disambiguationData":[OSD([sQuery(id+"F9.wireOp",EDGE,"E7")])]})});
            var Q1;
            Q1=makeQuery(id+"F10.boolean.opBoolean","COPY",FACE,{"disambiguationData":[TD([makeQuery(id+"F6.opExtrude","SWEPT_FACE",FACE,{"disambiguationData":[OSD([sQuery(id+"F5.wireOp",EDGE,"E5.sketch_text.stroke-28")])]})])],"derivedFrom":makeQuery(id+"F10.opExtrude","SWEPT_FACE",FACE,{"disambiguationData":[OSD([sQuery(id+"F9.wireOp",EDGE,"E7")])]})});
            var Q2;
            Q2=makeQuery(id+"F10.boolean.opBoolean","COPY",FACE,{"disambiguationData":[TD([makeQuery(id+"F6.opExtrude","SWEPT_FACE",FACE,{"disambiguationData":[OSD([sQuery(id+"F5.wireOp",EDGE,"E5.sketch_text.stroke-40")])]})])],"derivedFrom":makeQuery(id+"F10.opExtrude","SWEPT_FACE",FACE,{"disambiguationData":[OSD([sQuery(id+"F9.wireOp",EDGE,"E7")])]})});
            var Q3;
            Q3=makeQuery(id+"F10.boolean.opBoolean","COPY",FACE,{"disambiguationData":[TD([makeQuery(id+"F6.opExtrude","SWEPT_FACE",FACE,{"disambiguationData":[OSD([sQuery(id+"F5.wireOp",EDGE,"E5.sketch_text.stroke-52")])]})])],"derivedFrom":makeQuery(id+"F10.opExtrude","SWEPT_FACE",FACE,{"disambiguationData":[OSD([sQuery(id+"F9.wireOp",EDGE,"E7")])]})});
            var Q4;
            Q4=makeQuery(id+"F10.boolean.opBoolean","COPY",FACE,{"disambiguationData":[TD([makeQuery(id+"F6.opExtrude","SWEPT_FACE",FACE,{"disambiguationData":[OSD([sQuery(id+"F5.wireOp",EDGE,"E5.sketch_text.stroke-62")])]})])],"derivedFrom":makeQuery(id+"F10.opExtrude","SWEPT_FACE",FACE,{"disambiguationData":[OSD([sQuery(id+"F9.wireOp",EDGE,"E7")])]})});
            var Q5;
            Q5=makeQuery(id+"F10.boolean.opBoolean","COPY",FACE,{"disambiguationData":[TD([makeQuery(id+"F6.opExtrude","SWEPT_FACE",FACE,{"disambiguationData":[OSD([sQuery(id+"F5.wireOp",EDGE,"E5.sketch_text.stroke-70")])]})])],"derivedFrom":makeQuery(id+"F10.opExtrude","SWEPT_FACE",FACE,{"disambiguationData":[OSD([sQuery(id+"F9.wireOp",EDGE,"E7")])]})});
            var Q6;
            Q6=makeQuery(id+"F10.boolean.opBoolean","COPY",FACE,{"disambiguationData":[TD([makeQuery(id+"F6.opExtrude","SWEPT_FACE",FACE,{"disambiguationData":[OSD([sQuery(id+"F5.wireOp",EDGE,"E5.sketch_text.stroke-82")])]})])],"derivedFrom":makeQuery(id+"F10.opExtrude","SWEPT_FACE",FACE,{"disambiguationData":[OSD([sQuery(id+"F9.wireOp",EDGE,"E7")])]})});
            var Q7;
            Q7=makeQuery(id+"F10.boolean.opBoolean","COPY",FACE,{"disambiguationData":[TD([makeQuery(id+"F6.opExtrude","SWEPT_FACE",FACE,{"disambiguationData":[OSD([sQuery(id+"F5.wireOp",EDGE,"E5.sketch_text.stroke-101")])]})])],"derivedFrom":makeQuery(id+"F10.opExtrude","SWEPT_FACE",FACE,{"disambiguationData":[OSD([sQuery(id+"F9.wireOp",EDGE,"E7")])]})});
            var Q8;
            Q8=makeQuery(id+"F10.boolean.opBoolean","COPY",FACE,{"disambiguationData":[TD([makeQuery(id+"F6.opExtrude","SWEPT_FACE",FACE,{"disambiguationData":[OSD([sQuery(id+"F5.wireOp",EDGE,"E5.sketch_text.stroke-115")])]})])],"derivedFrom":makeQuery(id+"F10.opExtrude","SWEPT_FACE",FACE,{"disambiguationData":[OSD([sQuery(id+"F9.wireOp",EDGE,"E7")])]})});
            var Q9;
            Q9=makeQuery(id+"F10.boolean.opBoolean","COPY",FACE,{"disambiguationData":[TD([makeQuery(id+"F6.opExtrude","SWEPT_FACE",FACE,{"disambiguationData":[OSD([sQuery(id+"F5.wireOp",EDGE,"E5.sketch_text.stroke-127")])]})])],"derivedFrom":makeQuery(id+"F10.opExtrude","SWEPT_FACE",FACE,{"disambiguationData":[OSD([sQuery(id+"F9.wireOp",EDGE,"E7")])]})});
            var Q10;
            Q10=makeQuery(id+"F10.boolean.opBoolean","COPY",FACE,{"disambiguationData":[TD([makeQuery(id+"F6.opExtrude","SWEPT_FACE",FACE,{"disambiguationData":[OSD([sQuery(id+"F5.wireOp",EDGE,"E5.sketch_text.stroke-135")])]})])],"derivedFrom":makeQuery(id+"F10.opExtrude","SWEPT_FACE",FACE,{"disambiguationData":[OSD([sQuery(id+"F9.wireOp",EDGE,"E7")])]})});
            var Q11;
            Q11=makeQuery(id+"F10.boolean.opBoolean","COPY",FACE,{"disambiguationData":[TD([makeQuery(id+"F6.opExtrude","SWEPT_FACE",FACE,{"disambiguationData":[OSD([sQuery(id+"F5.wireOp",EDGE,"E5.sketch_text.stroke-139")])]})])],"derivedFrom":makeQuery(id+"F10.opExtrude","SWEPT_FACE",FACE,{"disambiguationData":[OSD([sQuery(id+"F9.wireOp",EDGE,"E7")])]})});
            var Q12;
            Q12=makeQuery(id+"F10.boolean.opBoolean","COPY",FACE,{"disambiguationData":[TD([makeQuery(id+"F6.opExtrude","SWEPT_FACE",FACE,{"disambiguationData":[OSD([sQuery(id+"F5.wireOp",EDGE,"E5.sketch_text.stroke-155")])]})])],"derivedFrom":makeQuery(id+"F10.opExtrude","SWEPT_FACE",FACE,{"disambiguationData":[OSD([sQuery(id+"F9.wireOp",EDGE,"E7")])]})});
            var Q13;
            {var subQ2=sQuery(id+"F5.wireOp",EDGE,"E5.sketch_text.stroke-108");Q13=makeQuery(id+"F10.boolean.opBoolean","INTERSECT",EDGE,{"derivedFrom":[makeQuery(id+"F6.boolean.opBoolean","SPLIT",FACE,{"disambiguationData":[TD([makeQuery(id+"F1.opExtrude","SWEPT_FACE",FACE,{"disambiguationData":[OSD([sQuery(id+"F0.wireOp",EDGE,"E0")])]})])],"derivedFrom":makeQuery(id+"F6.opExtrude","SWEPT_FACE",FACE,{"disambiguationData":[OSD([subQ2])]})}),makeQuery(id+"F10.opExtrude","SWEPT_FACE",FACE,{"disambiguationData":[OSD([sQuery(id+"F9.wireOp",EDGE,"E7")])]})]});}
            var Q14;
            {var subQ2=sQuery(id+"F5.wireOp",EDGE,"E5.sketch_text.stroke-107");Q14=makeQuery(id+"F10.boolean.opBoolean","INTERSECT",EDGE,{"derivedFrom":[makeQuery(id+"F6.boolean.opBoolean","SPLIT",FACE,{"disambiguationData":[TD([makeQuery(id+"F1.opExtrude","SWEPT_FACE",FACE,{"disambiguationData":[OSD([sQuery(id+"F0.wireOp",EDGE,"E0")])]})])],"derivedFrom":makeQuery(id+"F6.opExtrude","SWEPT_FACE",FACE,{"disambiguationData":[OSD([subQ2])]})}),makeQuery(id+"F10.opExtrude","SWEPT_FACE",FACE,{"disambiguationData":[OSD([sQuery(id+"F9.wireOp",EDGE,"E7")])]})]});}
            var Q15;
            {var subQ1=sQuery(id+"F5.wireOp",EDGE,"E5.sketch_text.stroke-106");Q15=makeQuery(id+"F10.boolean.opBoolean","INTERSECT",EDGE,{"derivedFrom":[makeQuery(id+"F6.boolean.opBoolean","SPLIT",FACE,{"disambiguationData":[TD([makeQuery(id+"F1.opExtrude","SWEPT_FACE",FACE,{"disambiguationData":[OSD([sQuery(id+"F0.wireOp",EDGE,"E0")])]})])],"derivedFrom":makeQuery(id+"F6.opExtrude","SWEPT_FACE",FACE,{"disambiguationData":[OSD([subQ1])]})}),makeQuery(id+"F10.opExtrude","SWEPT_FACE",FACE,{"disambiguationData":[OSD([sQuery(id+"F9.wireOp",EDGE,"E7")])]})]});}
            var Q16;
            {var subQ1=sQuery(id+"F5.wireOp",EDGE,"E5.sketch_text.stroke-109");Q16=makeQuery(id+"F10.boolean.opBoolean","INTERSECT",EDGE,{"derivedFrom":[makeQuery(id+"F6.boolean.opBoolean","SPLIT",FACE,{"disambiguationData":[TD([makeQuery(id+"F1.opExtrude","SWEPT_FACE",FACE,{"disambiguationData":[OSD([sQuery(id+"F0.wireOp",EDGE,"E0")])]})])],"derivedFrom":makeQuery(id+"F6.opExtrude","SWEPT_FACE",FACE,{"disambiguationData":[OSD([subQ1])]})}),makeQuery(id+"F10.opExtrude","SWEPT_FACE",FACE,{"disambiguationData":[OSD([sQuery(id+"F9.wireOp",EDGE,"E7")])]})]});}
            var Q17;
            {var subQ2=sQuery(id+"F5.wireOp",EDGE,"E5.sketch_text.stroke-105");Q17=makeQuery(id+"F10.boolean.opBoolean","INTERSECT",EDGE,{"derivedFrom":[makeQuery(id+"F6.boolean.opBoolean","SPLIT",FACE,{"disambiguationData":[TD([makeQuery(id+"F1.opExtrude","SWEPT_FACE",FACE,{"disambiguationData":[OSD([sQuery(id+"F0.wireOp",EDGE,"E0")])]})])],"derivedFrom":makeQuery(id+"F6.opExtrude","SWEPT_FACE",FACE,{"disambiguationData":[OSD([subQ2])]})}),makeQuery(id+"F10.opExtrude","SWEPT_FACE",FACE,{"disambiguationData":[OSD([sQuery(id+"F9.wireOp",EDGE,"E7")])]})]});}
            var Q18;
            {var subQ2=sQuery(id+"F5.wireOp",EDGE,"E5.sketch_text.stroke-110");Q18=makeQuery(id+"F10.boolean.opBoolean","INTERSECT",EDGE,{"derivedFrom":[makeQuery(id+"F6.boolean.opBoolean","SPLIT",FACE,{"disambiguationData":[TD([makeQuery(id+"F1.opExtrude","SWEPT_FACE",FACE,{"disambiguationData":[OSD([sQuery(id+"F0.wireOp",EDGE,"E0")])]})])],"derivedFrom":makeQuery(id+"F6.opExtrude","SWEPT_FACE",FACE,{"disambiguationData":[OSD([subQ2])]})}),makeQuery(id+"F10.opExtrude","SWEPT_FACE",FACE,{"disambiguationData":[OSD([sQuery(id+"F9.wireOp",EDGE,"E7")])]})]});}
            fillet(context, id + "F20", {"entities" : qUnion([Q0, Q1, Q2, Q3, Q4, Q5, Q6, Q7, Q8, Q9, Q10, Q11, Q12, Q13, Q14, Q15, Q16, Q17, Q18]), "radius" : 0.25 * mm, "tangentPropagation" : true, "allowEdgeOverflow" : false});
        }
        {
            var Q0;
            {var subQ0=sQuery(id+"F5.wireOp",EDGE,"E5.sketch_text.stroke-114");Q0=makeQuery(id+"F10.boolean.opBoolean","INTERSECT",EDGE,{"derivedFrom":[makeQuery(id+"F6.boolean.opBoolean","SPLIT",FACE,{"disambiguationData":[TD([makeQuery(id+"F1.opExtrude","SWEPT_FACE",FACE,{"disambiguationData":[OSD([sQuery(id+"F0.wireOp",EDGE,"E0")])]})])],"derivedFrom":makeQuery(id+"F6.opExtrude","SWEPT_FACE",FACE,{"disambiguationData":[OSD([subQ0])]})}),makeQuery(id+"F10.opExtrude","SWEPT_FACE",FACE,{"disambiguationData":[OSD([sQuery(id+"F9.wireOp",EDGE,"E7")])]})]});}
            fillet(context, id + "F21", {"entities" : qUnion([Q0]), "radius" : 0.25 * mm, "tangentPropagation" : true, "allowEdgeOverflow" : false});
        }
        {
            var Q0;
            Q0=makeQuery(id+"F1.opExtrude","CAP_FACE",FACE,{"disambiguationData":[OSD([sQuery(id+"F0.wireOp",EDGE,"E0")])],"isStart":false});
            var sketch = newSketch(context, id + "F22", { "sketchPlane" : qUnion([Q0])});
            skText(sketch, "E18", { "text": "FILL", "fontName": "OpenSans-Bold.ttf"});
            skText(sketch, "E19", { "text": "ME", "fontName": "OpenSans-Bold.ttf"});
            const initialGuessF22  = {"E18": [-0.0089, 0.00027, 1, 0, 0.00635], "E19": [-0.00662, -0.00813, 1, 0, 0.00635]};
            skSetInitialGuess(sketch, initialGuessF22);
            skSolve(sketch);
        }
        {
            var Q0;
            Q0 = qSketchRegion(id + "F22", true);
            extrude(context, id + "F23", {"entities" : qUnion([Q0]), "operationType" : NewBodyOperationType.ADD, "depth" : 1.02 * mm});
        }
    });
